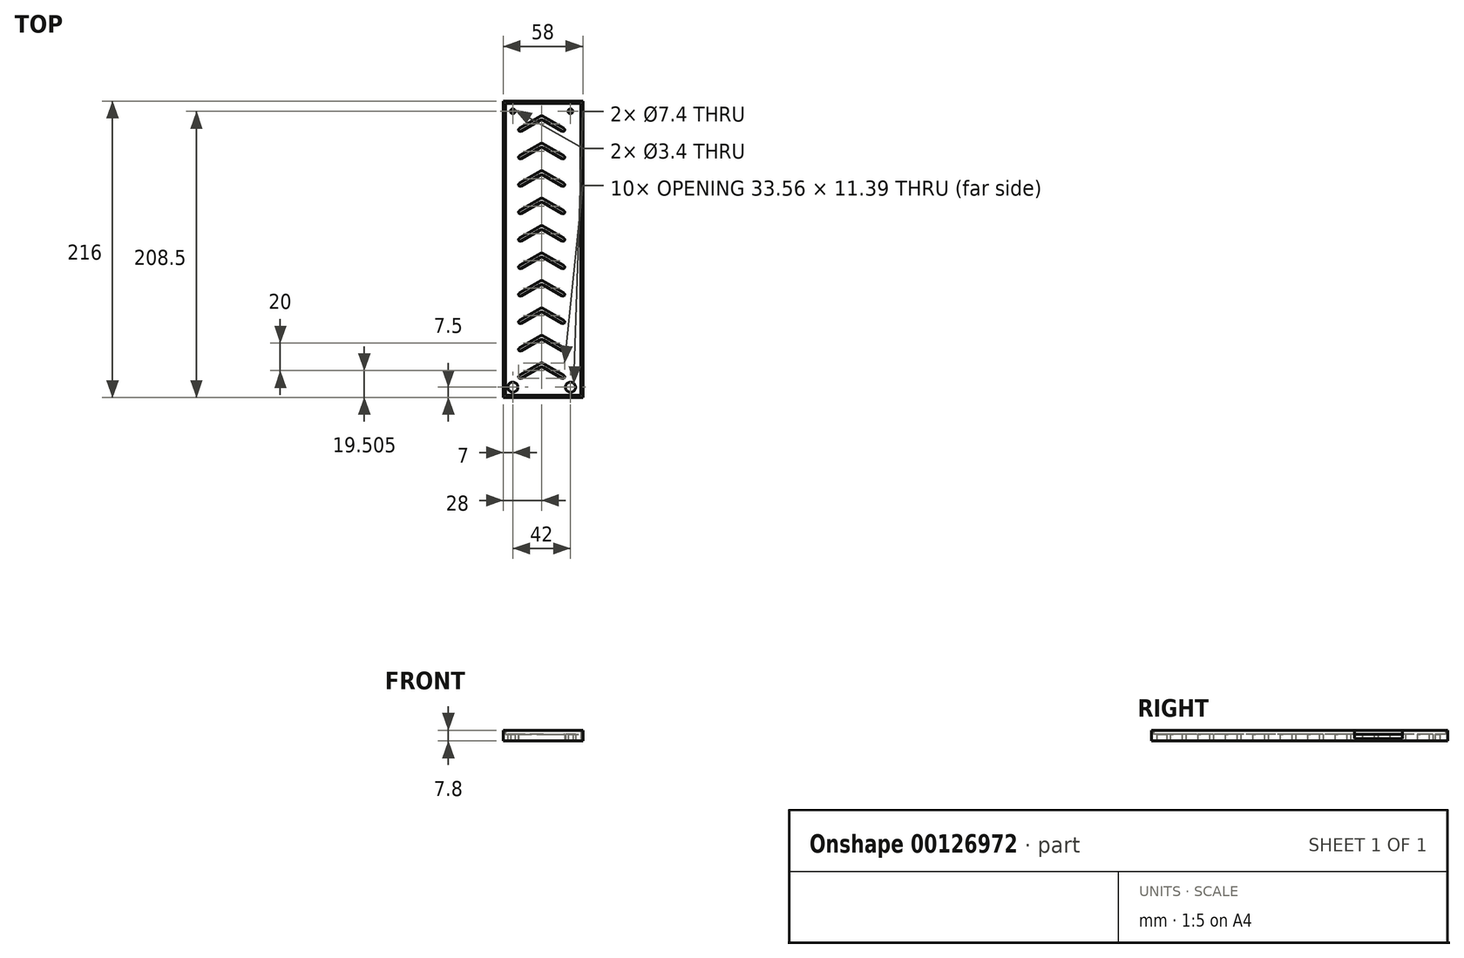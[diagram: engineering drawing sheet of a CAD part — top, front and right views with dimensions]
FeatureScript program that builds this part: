
annotation { "Feature Type Name" : "Feature", "Feature Type Description" : "" }
export const myFeature = defineFeature(function(context is Context, id is Id, definition is map)
    precondition{}
    {
        {
            var Q0;
            Q0=qCreatedBy(makeId("Top.planeOp"),FACE);
            var sketch = newSketch(context, id + "F0", { "sketchPlane" : qUnion([Q0])});
            skLineSegment(sketch, "E0.bottom", {"start": v(0, 0) * mm, "end": v(58, 0) * mm});
            skLineSegment(sketch, "E0.top", {"start": v(0, -216) * mm, "end": v(58, -216) * mm});
            skLineSegment(sketch, "E0.left", {"start": v(0, 0) * mm, "end": v(0, -216) * mm});
            skLineSegment(sketch, "E0.right", {"start": v(58, 0) * mm, "end": v(58, -216) * mm});
            skLineSegment(sketch, "E1.0", {"start": v(1.6, -1.6) * mm, "end": v(1.6, -214.4) * mm});
            skLineSegment(sketch, "E1.1", {"start": v(1.6, -1.6) * mm, "end": v(56.4, -1.6) * mm});
            skLineSegment(sketch, "E1.2", {"start": v(56.4, -1.6) * mm, "end": v(56.4, -214.4) * mm});
            skLineSegment(sketch, "E1.3", {"start": v(1.6, -214.4) * mm, "end": v(56.4, -214.4) * mm});
            skLineSegment(sketch, "E2", {"start": v(28, 48.15) * mm, "end": v(28, -228.16) * mm, "construction": true});
            skLineSegment(sketch, "E3", {"start": v(-41.33, -108) * mm, "end": v(141.9, -108) * mm, "construction": true});
            skCircle(sketch, "E4", {"center": v(7, -7.5) * mm, "radius": 1.7 * mm});
            skCircle(sketch, "E5", {"center": v(49, -7.5) * mm, "radius": 1.7 * mm});
            skLineSegment(sketch, "E6", {"start": v(7, -7.5) * mm, "end": v(49, -7.5) * mm, "construction": true});
            skLineSegment(sketch, "E7", {"start": v(56.4, -68) * mm, "end": v(58, -68) * mm});
            skLineSegment(sketch, "E8", {"start": v(56.4, -33) * mm, "end": v(58, -33) * mm});
            skCircle(sketch, "E9.0", {"center": v(7, -7.5) * mm, "radius": 3.7 * mm});
            skCircle(sketch, "E10.0", {"center": v(49, -7.5) * mm, "radius": 3.7 * mm});
            skLineSegment(sketch, "E11", {"start": v(28, -12) * mm, "end": v(43.59, -21) * mm, "construction": true});
            skLineSegment(sketch, "E12.MirrorCS", {"start": v(28, -12) * mm, "end": v(12.41, -21) * mm, "construction": true});
            skArc(sketch, "E13.0.startCap", {"start": v(27.4, -10.96) * mm, "mid": v(28, -10.8) * mm, "end": v(28.6, -10.96) * mm});
            skArc(sketch, "E13.0.endCap", {"start": v(13.01, -22.04) * mm, "mid": v(11.37, -21.6) * mm, "end": v(11.81, -19.96) * mm});
            skLineSegment(sketch, "E13.0.left", {"start": v(26.8, -14.08) * mm, "end": v(13.01, -22.04) * mm});
            skLineSegment(sketch, "E13.0.right", {"start": v(27.4, -10.96) * mm, "end": v(11.81, -19.96) * mm});
            skArc(sketch, "E13.1.endCap", {"start": v(44.19, -19.96) * mm, "mid": v(44.63, -21.6) * mm, "end": v(42.99, -22.04) * mm});
            skLineSegment(sketch, "E13.1.left", {"start": v(28.6, -10.96) * mm, "end": v(44.19, -19.96) * mm});
            skLineSegment(sketch, "E13.1.right", {"start": v(29.2, -14.08) * mm, "end": v(42.99, -22.04) * mm});
            skPoint(sketch, "E14.visualSharp", {"position": v(28, -13.39) * mm});
            skArc(sketch, "E14.filletArc", {"start": v(29.2, -14.08) * mm, "mid": v(28, -13.76) * mm, "end": v(26.8, -14.08) * mm});
            skLineSegment(sketch, "E15.1.0.0", {"start": v(28, -32) * mm, "end": v(12.41, -41) * mm, "construction": true});
            skLineSegment(sketch, "E15.1.0.1", {"start": v(28, -32) * mm, "end": v(43.59, -41) * mm, "construction": true});
            skArc(sketch, "E15.1.0.2", {"start": v(27.4, -30.96) * mm, "mid": v(28, -30.8) * mm, "end": v(28.6, -30.96) * mm});
            skLineSegment(sketch, "E15.1.0.3", {"start": v(26.8, -34.08) * mm, "end": v(13.01, -42.04) * mm});
            skLineSegment(sketch, "E15.1.0.4", {"start": v(28.6, -30.96) * mm, "end": v(44.19, -39.96) * mm});
            skPoint(sketch, "E15.1.0.5", {"position": v(28, -33.39) * mm});
            skArc(sketch, "E15.1.0.6", {"start": v(13.01, -42.04) * mm, "mid": v(11.37, -41.6) * mm, "end": v(11.81, -39.96) * mm});
            skLineSegment(sketch, "E15.1.0.7", {"start": v(27.4, -30.96) * mm, "end": v(11.81, -39.96) * mm});
            skLineSegment(sketch, "E15.1.0.8", {"start": v(29.2, -34.08) * mm, "end": v(42.99, -42.04) * mm});
            skArc(sketch, "E15.1.0.9", {"start": v(44.19, -39.96) * mm, "mid": v(44.63, -41.6) * mm, "end": v(42.99, -42.04) * mm});
            skArc(sketch, "E15.1.0.10", {"start": v(29.2, -34.08) * mm, "mid": v(28, -33.76) * mm, "end": v(26.8, -34.08) * mm});
            skLineSegment(sketch, "E15.2.0.0", {"start": v(28, -52) * mm, "end": v(12.41, -61) * mm, "construction": true});
            skLineSegment(sketch, "E15.2.0.1", {"start": v(28, -52) * mm, "end": v(43.59, -61) * mm, "construction": true});
            skArc(sketch, "E15.2.0.2", {"start": v(27.4, -50.96) * mm, "mid": v(28, -50.8) * mm, "end": v(28.6, -50.96) * mm});
            skLineSegment(sketch, "E15.2.0.3", {"start": v(26.8, -54.08) * mm, "end": v(13.01, -62.04) * mm});
            skLineSegment(sketch, "E15.2.0.4", {"start": v(28.6, -50.96) * mm, "end": v(44.19, -59.96) * mm});
            skPoint(sketch, "E15.2.0.5", {"position": v(28, -53.39) * mm});
            skArc(sketch, "E15.2.0.6", {"start": v(13.01, -62.04) * mm, "mid": v(11.37, -61.6) * mm, "end": v(11.81, -59.96) * mm});
            skLineSegment(sketch, "E15.2.0.7", {"start": v(27.4, -50.96) * mm, "end": v(11.81, -59.96) * mm});
            skLineSegment(sketch, "E15.2.0.8", {"start": v(29.2, -54.08) * mm, "end": v(42.99, -62.04) * mm});
            skArc(sketch, "E15.2.0.9", {"start": v(44.19, -59.96) * mm, "mid": v(44.63, -61.6) * mm, "end": v(42.99, -62.04) * mm});
            skArc(sketch, "E15.2.0.10", {"start": v(29.2, -54.08) * mm, "mid": v(28, -53.76) * mm, "end": v(26.8, -54.08) * mm});
            skLineSegment(sketch, "E15.3.0.0", {"start": v(28, -72) * mm, "end": v(12.41, -81) * mm, "construction": true});
            skLineSegment(sketch, "E15.3.0.1", {"start": v(28, -72) * mm, "end": v(43.59, -81) * mm, "construction": true});
            skArc(sketch, "E15.3.0.2", {"start": v(27.4, -70.96) * mm, "mid": v(28, -70.8) * mm, "end": v(28.6, -70.96) * mm});
            skLineSegment(sketch, "E15.3.0.3", {"start": v(26.8, -74.08) * mm, "end": v(13.01, -82.04) * mm});
            skLineSegment(sketch, "E15.3.0.4", {"start": v(28.6, -70.96) * mm, "end": v(44.19, -79.96) * mm});
            skPoint(sketch, "E15.3.0.5", {"position": v(28, -73.39) * mm});
            skArc(sketch, "E15.3.0.6", {"start": v(13.01, -82.04) * mm, "mid": v(11.37, -81.6) * mm, "end": v(11.81, -79.96) * mm});
            skLineSegment(sketch, "E15.3.0.7", {"start": v(27.4, -70.96) * mm, "end": v(11.81, -79.96) * mm});
            skLineSegment(sketch, "E15.3.0.8", {"start": v(29.2, -74.08) * mm, "end": v(42.99, -82.04) * mm});
            skArc(sketch, "E15.3.0.9", {"start": v(44.19, -79.96) * mm, "mid": v(44.63, -81.6) * mm, "end": v(42.99, -82.04) * mm});
            skArc(sketch, "E15.3.0.10", {"start": v(29.2, -74.08) * mm, "mid": v(28, -73.76) * mm, "end": v(26.8, -74.08) * mm});
            skLineSegment(sketch, "E15.4.0.0", {"start": v(28, -92) * mm, "end": v(12.41, -101) * mm, "construction": true});
            skLineSegment(sketch, "E15.4.0.1", {"start": v(28, -92) * mm, "end": v(43.59, -101) * mm, "construction": true});
            skArc(sketch, "E15.4.0.2", {"start": v(27.4, -90.96) * mm, "mid": v(28, -90.8) * mm, "end": v(28.6, -90.96) * mm});
            skLineSegment(sketch, "E15.4.0.3", {"start": v(26.8, -94.08) * mm, "end": v(13.01, -102.04) * mm});
            skLineSegment(sketch, "E15.4.0.4", {"start": v(28.6, -90.96) * mm, "end": v(44.19, -99.96) * mm});
            skPoint(sketch, "E15.4.0.5", {"position": v(28, -93.39) * mm});
            skArc(sketch, "E15.4.0.6", {"start": v(13.01, -102.04) * mm, "mid": v(11.37, -101.6) * mm, "end": v(11.81, -99.96) * mm});
            skLineSegment(sketch, "E15.4.0.7", {"start": v(27.4, -90.96) * mm, "end": v(11.81, -99.96) * mm});
            skLineSegment(sketch, "E15.4.0.8", {"start": v(29.2, -94.08) * mm, "end": v(42.99, -102.04) * mm});
            skArc(sketch, "E15.4.0.9", {"start": v(44.19, -99.96) * mm, "mid": v(44.63, -101.6) * mm, "end": v(42.99, -102.04) * mm});
            skArc(sketch, "E15.4.0.10", {"start": v(29.2, -94.08) * mm, "mid": v(28, -93.76) * mm, "end": v(26.8, -94.08) * mm});
            skLineSegment(sketch, "E15.5.0.0", {"start": v(28, -112) * mm, "end": v(12.41, -121) * mm, "construction": true});
            skLineSegment(sketch, "E15.5.0.1", {"start": v(28, -112) * mm, "end": v(43.59, -121) * mm, "construction": true});
            skArc(sketch, "E15.5.0.2", {"start": v(27.4, -110.96) * mm, "mid": v(28, -110.8) * mm, "end": v(28.6, -110.96) * mm});
            skLineSegment(sketch, "E15.5.0.3", {"start": v(26.8, -114.08) * mm, "end": v(13.01, -122.04) * mm});
            skLineSegment(sketch, "E15.5.0.4", {"start": v(28.6, -110.96) * mm, "end": v(44.19, -119.96) * mm});
            skPoint(sketch, "E15.5.0.5", {"position": v(28, -113.39) * mm});
            skArc(sketch, "E15.5.0.6", {"start": v(13.01, -122.04) * mm, "mid": v(11.37, -121.6) * mm, "end": v(11.81, -119.96) * mm});
            skLineSegment(sketch, "E15.5.0.7", {"start": v(27.4, -110.96) * mm, "end": v(11.81, -119.96) * mm});
            skLineSegment(sketch, "E15.5.0.8", {"start": v(29.2, -114.08) * mm, "end": v(42.99, -122.04) * mm});
            skArc(sketch, "E15.5.0.9", {"start": v(44.19, -119.96) * mm, "mid": v(44.63, -121.6) * mm, "end": v(42.99, -122.04) * mm});
            skArc(sketch, "E15.5.0.10", {"start": v(29.2, -114.08) * mm, "mid": v(28, -113.76) * mm, "end": v(26.8, -114.08) * mm});
            skLineSegment(sketch, "E15.6.0.0", {"start": v(28, -132) * mm, "end": v(12.41, -141) * mm, "construction": true});
            skLineSegment(sketch, "E15.6.0.1", {"start": v(28, -132) * mm, "end": v(43.59, -141) * mm, "construction": true});
            skArc(sketch, "E15.6.0.2", {"start": v(27.4, -130.96) * mm, "mid": v(28, -130.8) * mm, "end": v(28.6, -130.96) * mm});
            skLineSegment(sketch, "E15.6.0.3", {"start": v(26.8, -134.08) * mm, "end": v(13.01, -142.04) * mm});
            skLineSegment(sketch, "E15.6.0.4", {"start": v(28.6, -130.96) * mm, "end": v(44.19, -139.96) * mm});
            skPoint(sketch, "E15.6.0.5", {"position": v(28, -133.39) * mm});
            skArc(sketch, "E15.6.0.6", {"start": v(13.01, -142.04) * mm, "mid": v(11.37, -141.6) * mm, "end": v(11.81, -139.96) * mm});
            skLineSegment(sketch, "E15.6.0.7", {"start": v(27.4, -130.96) * mm, "end": v(11.81, -139.96) * mm});
            skLineSegment(sketch, "E15.6.0.8", {"start": v(29.2, -134.08) * mm, "end": v(42.99, -142.04) * mm});
            skArc(sketch, "E15.6.0.9", {"start": v(44.19, -139.96) * mm, "mid": v(44.63, -141.6) * mm, "end": v(42.99, -142.04) * mm});
            skArc(sketch, "E15.6.0.10", {"start": v(29.2, -134.08) * mm, "mid": v(28, -133.76) * mm, "end": v(26.8, -134.08) * mm});
            skLineSegment(sketch, "E15.7.0.0", {"start": v(28, -152) * mm, "end": v(12.41, -161) * mm, "construction": true});
            skLineSegment(sketch, "E15.7.0.1", {"start": v(28, -152) * mm, "end": v(43.59, -161) * mm, "construction": true});
            skArc(sketch, "E15.7.0.2", {"start": v(27.4, -150.96) * mm, "mid": v(28, -150.8) * mm, "end": v(28.6, -150.96) * mm});
            skLineSegment(sketch, "E15.7.0.3", {"start": v(26.8, -154.08) * mm, "end": v(13.01, -162.04) * mm});
            skLineSegment(sketch, "E15.7.0.4", {"start": v(28.6, -150.96) * mm, "end": v(44.19, -159.96) * mm});
            skPoint(sketch, "E15.7.0.5", {"position": v(28, -153.39) * mm});
            skArc(sketch, "E15.7.0.6", {"start": v(13.01, -162.04) * mm, "mid": v(11.37, -161.6) * mm, "end": v(11.81, -159.96) * mm});
            skLineSegment(sketch, "E15.7.0.7", {"start": v(27.4, -150.96) * mm, "end": v(11.81, -159.96) * mm});
            skLineSegment(sketch, "E15.7.0.8", {"start": v(29.2, -154.08) * mm, "end": v(42.99, -162.04) * mm});
            skArc(sketch, "E15.7.0.9", {"start": v(44.19, -159.96) * mm, "mid": v(44.63, -161.6) * mm, "end": v(42.99, -162.04) * mm});
            skArc(sketch, "E15.7.0.10", {"start": v(29.2, -154.08) * mm, "mid": v(28, -153.76) * mm, "end": v(26.8, -154.08) * mm});
            skLineSegment(sketch, "E15.8.0.0", {"start": v(28, -172) * mm, "end": v(12.41, -181) * mm, "construction": true});
            skLineSegment(sketch, "E15.8.0.1", {"start": v(28, -172) * mm, "end": v(43.59, -181) * mm, "construction": true});
            skArc(sketch, "E15.8.0.2", {"start": v(27.4, -170.96) * mm, "mid": v(28, -170.8) * mm, "end": v(28.6, -170.96) * mm});
            skLineSegment(sketch, "E15.8.0.3", {"start": v(26.8, -174.08) * mm, "end": v(13.01, -182.04) * mm});
            skLineSegment(sketch, "E15.8.0.4", {"start": v(28.6, -170.96) * mm, "end": v(44.19, -179.96) * mm});
            skPoint(sketch, "E15.8.0.5", {"position": v(28, -173.39) * mm});
            skArc(sketch, "E15.8.0.6", {"start": v(13.01, -182.04) * mm, "mid": v(11.37, -181.6) * mm, "end": v(11.81, -179.96) * mm});
            skLineSegment(sketch, "E15.8.0.7", {"start": v(27.4, -170.96) * mm, "end": v(11.81, -179.96) * mm});
            skLineSegment(sketch, "E15.8.0.8", {"start": v(29.2, -174.08) * mm, "end": v(42.99, -182.04) * mm});
            skArc(sketch, "E15.8.0.9", {"start": v(44.19, -179.96) * mm, "mid": v(44.63, -181.6) * mm, "end": v(42.99, -182.04) * mm});
            skArc(sketch, "E15.8.0.10", {"start": v(29.2, -174.08) * mm, "mid": v(28, -173.76) * mm, "end": v(26.8, -174.08) * mm});
            skLineSegment(sketch, "E15.9.0.0", {"start": v(28, -192) * mm, "end": v(12.41, -201) * mm, "construction": true});
            skLineSegment(sketch, "E15.9.0.1", {"start": v(28, -192) * mm, "end": v(43.59, -201) * mm, "construction": true});
            skArc(sketch, "E15.9.0.2", {"start": v(27.4, -190.96) * mm, "mid": v(28, -190.8) * mm, "end": v(28.6, -190.96) * mm});
            skLineSegment(sketch, "E15.9.0.3", {"start": v(26.8, -194.08) * mm, "end": v(13.01, -202.04) * mm});
            skLineSegment(sketch, "E15.9.0.4", {"start": v(28.6, -190.96) * mm, "end": v(44.19, -199.96) * mm});
            skPoint(sketch, "E15.9.0.5", {"position": v(28, -193.39) * mm});
            skArc(sketch, "E15.9.0.6", {"start": v(13.01, -202.04) * mm, "mid": v(11.37, -201.6) * mm, "end": v(11.81, -199.96) * mm});
            skLineSegment(sketch, "E15.9.0.7", {"start": v(27.4, -190.96) * mm, "end": v(11.81, -199.96) * mm});
            skLineSegment(sketch, "E15.9.0.8", {"start": v(29.2, -194.08) * mm, "end": v(42.99, -202.04) * mm});
            skArc(sketch, "E15.9.0.9", {"start": v(44.19, -199.96) * mm, "mid": v(44.63, -201.6) * mm, "end": v(42.99, -202.04) * mm});
            skArc(sketch, "E15.9.0.10", {"start": v(29.2, -194.08) * mm, "mid": v(28, -193.76) * mm, "end": v(26.8, -194.08) * mm});
            skLineSegment(sketch, "E15.direction1", {"start": v(28, -12) * mm, "end": v(28, -32) * mm, "construction": true});
            skCircle(sketch, "E16.MirrorC", {"center": v(49, -208.5) * mm, "radius": 3.7 * mm});
            skCircle(sketch, "E17.MirrorC", {"center": v(49, -208.5) * mm, "radius": 1.7 * mm});
            skCircle(sketch, "E18.MirrorC", {"center": v(7, -208.5) * mm, "radius": 3.7 * mm});
            skCircle(sketch, "E19.MirrorC", {"center": v(7, -208.5) * mm, "radius": 1.7 * mm});
            skLineSegment(sketch, "E20", {"start": v(43.59, -21) * mm, "end": v(43.59, -201) * mm, "construction": true});
            skSolve(sketch);
        }
        {
            var Q0;
            Q0=makeQuery(id+"F0.imprint","IMPRINT",FACE,{"disambiguationData":[TD([[makeQuery(id+"F0.imprint","IMPRINT",EDGE,{"derivedFrom":sQuery(id+"F0.wireOp",EDGE,"E1.0")}),1.0]])]});
            var Q1;
            {var subQ0=sQuery(id+"F0.wireOp",EDGE,"E7");Q1=makeQuery(id+"F0.imprint","IMPRINT",FACE,{"disambiguationData":[TD([[makeQuery(id+"F0.imprint","IMPRINT",EDGE,{"derivedFrom":subQ0}),1.0]])]});}
            extrude(context, id + "F1", {"entities" : qUnion([Q0, Q1]), "depth" : 1.8 * mm});
        }
        {
            var Q0;
            Q0=makeQuery(id+"F0.imprint","IMPRINT",FACE,{"disambiguationData":[TD([[makeQuery(id+"F0.imprint","IMPRINT",EDGE,{"derivedFrom":sQuery(id+"F0.wireOp",EDGE,"E4")}),-1.0]])]});
            var Q1;
            Q1=makeQuery(id+"F0.imprint","IMPRINT",FACE,{"disambiguationData":[TD([[makeQuery(id+"F0.imprint","IMPRINT",EDGE,{"derivedFrom":sQuery(id+"F0.wireOp",EDGE,"E5")}),-1.0]])]});
            var Q2;
            Q2=makeQuery(id+"F0.imprint","IMPRINT",FACE,{"disambiguationData":[TD([[makeQuery(id+"F0.imprint","IMPRINT",EDGE,{"derivedFrom":sQuery(id+"F0.wireOp",EDGE,"E16.MirrorC")}),-1.0]])]});
            var Q3;
            Q3=makeQuery(id+"F0.imprint","IMPRINT",FACE,{"disambiguationData":[TD([[makeQuery(id+"F0.imprint","IMPRINT",EDGE,{"derivedFrom":sQuery(id+"F0.wireOp",EDGE,"E18.MirrorC")}),-1.0]])]});
            extrude(context, id + "F2", {"entities" : qUnion([Q0, Q1, Q2, Q3]), "operationType" : NewBodyOperationType.ADD, "depth" : 4.8 * mm});
        }
        {
            var Q0;
            {var subQ2=sQuery(id+"F0.wireOp",EDGE,"E0.bottom");Q0=makeQuery(id+"F0.imprint","IMPRINT",FACE,{"disambiguationData":[TD([[makeQuery(id+"F0.imprint","IMPRINT",EDGE,{"derivedFrom":subQ2}),-1.0]])]});}
            extrude(context, id + "F3", {"entities" : qUnion([Q0]), "operationType" : NewBodyOperationType.ADD, "depth" : 7.8 * mm});
        }
    });
